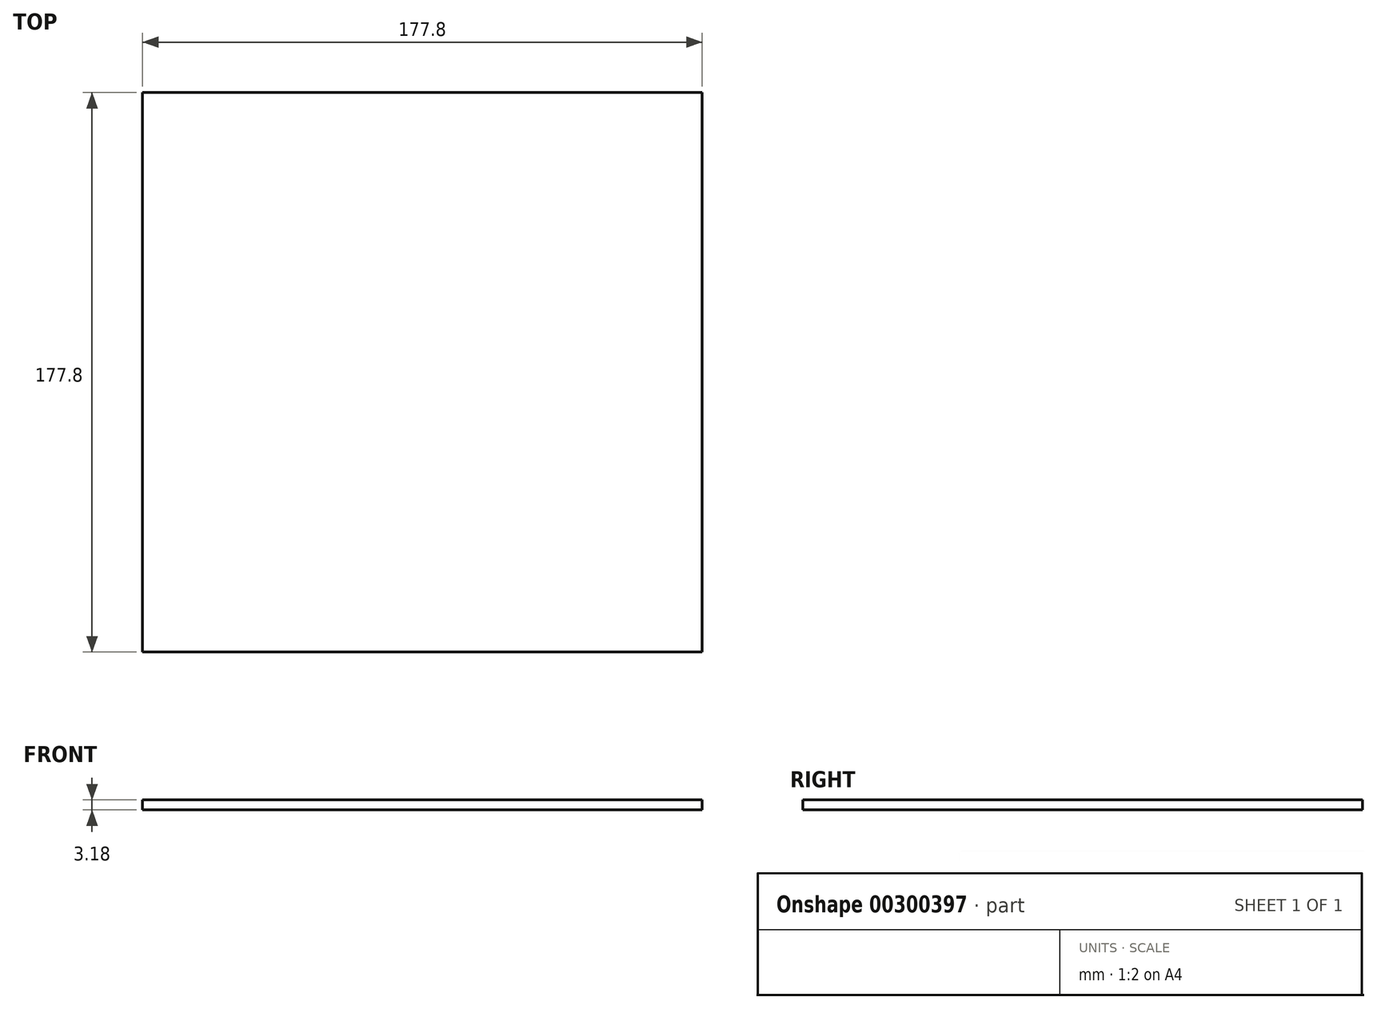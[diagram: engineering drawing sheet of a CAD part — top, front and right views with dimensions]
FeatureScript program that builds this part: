
annotation { "Feature Type Name" : "Feature", "Feature Type Description" : "" }
export const myFeature = defineFeature(function(context is Context, id is Id, definition is map)
    precondition{}
    {
        {
            var Q0;
            Q0=qCreatedBy(makeId("Top.planeOp"),FACE);
            var sketch = newSketch(context, id + "F0", { "sketchPlane" : qUnion([Q0])});
            skLineSegment(sketch, "E0.bottom", {"start": v(-88.9, 88.9) * mm, "end": v(88.9, 88.9) * mm});
            skLineSegment(sketch, "E0.top", {"start": v(-88.9, -88.9) * mm, "end": v(88.9, -88.9) * mm});
            skLineSegment(sketch, "E0.left", {"start": v(-88.9, 88.9) * mm, "end": v(-88.9, -88.9) * mm});
            skLineSegment(sketch, "E0.right", {"start": v(88.9, 88.9) * mm, "end": v(88.9, -88.9) * mm});
            skPoint(sketch, "E0.middle", {"position": v(0, 0) * mm});
            skSolve(sketch);
        }
        {
            var Q0;
            Q0 = qSketchRegion(id + "F0", true);
            extrude(context, id + "F1", {"entities" : qUnion([Q0]), "endBound" : BoundingType.SYMMETRIC, "depth" : 3.17 * mm});
        }
    });
